# Revit family: DPL_Ceiling
name_source: partatom
category: Lighting Fixtures
units: mm (PartAtom-declared; Revit-internal decimal feet)

## family parameters
Cut with Voids When Loaded = No
Host = Face
Light Source = No
OmniClass Number = 23.80.70.11.21
OmniClass Title = Emergency Lighting
Part Type = Normal
Room Calculation Point = No
Round Connector Dimension = Use Diameter
Shared = No

## types (2) — shared parameters
A = Yes
Apparent Load = 4 VA
Application = The Sempra® MR Series are a set of compact, low-profile Master/
Remote exit sign featuring cast aluminum construction. It allows for
easy installation and has energy saving, long-life LED lamps.
Certification = UL 924 Listed
NFPA 101 Life Safety Code
CEC T20 Compliant
Default Elevation = 48.000"
Description = The DPL Series of photoluminescent exit signage offers exit compliance with UL listed legible viewing distances of 50', 75' and 100'. The DPL photoluminescent exit signs do not require AC or electrical power. ALl signs have a 25 year lifecycle.
End = C : C1
Features = Available in Aluminum Frame, ABS Thermoplastic, Poly-Metal or Acrylic Construction
Maintenance Free Exit Compliance
No Electricity Required
Quick Installation
Made in USA
Wall, Ceiling or End Mount
UL924 Listed
Finish = White
Glass = light Glass
Holder Material = Steel
Lamp = LED Lamp
Lens = Red Glass
Load Classification = Lighting
Manufacturer = DUAL-LITE
Model = DPL
P = No
Type Comments = Exit Light
URL = https://www.currentlighting.com
Wall Plate Material = Black
Warranty = 5 Year Full
Wattage Comments = 3.72 W
Watts = 4 W

## type names (no varying parameters)
- DPL_P
- DPL_A

## geometry (parser evidence)
native form markers: Blend x8, Sweep x4
no freeform markers — native parametric forms only
